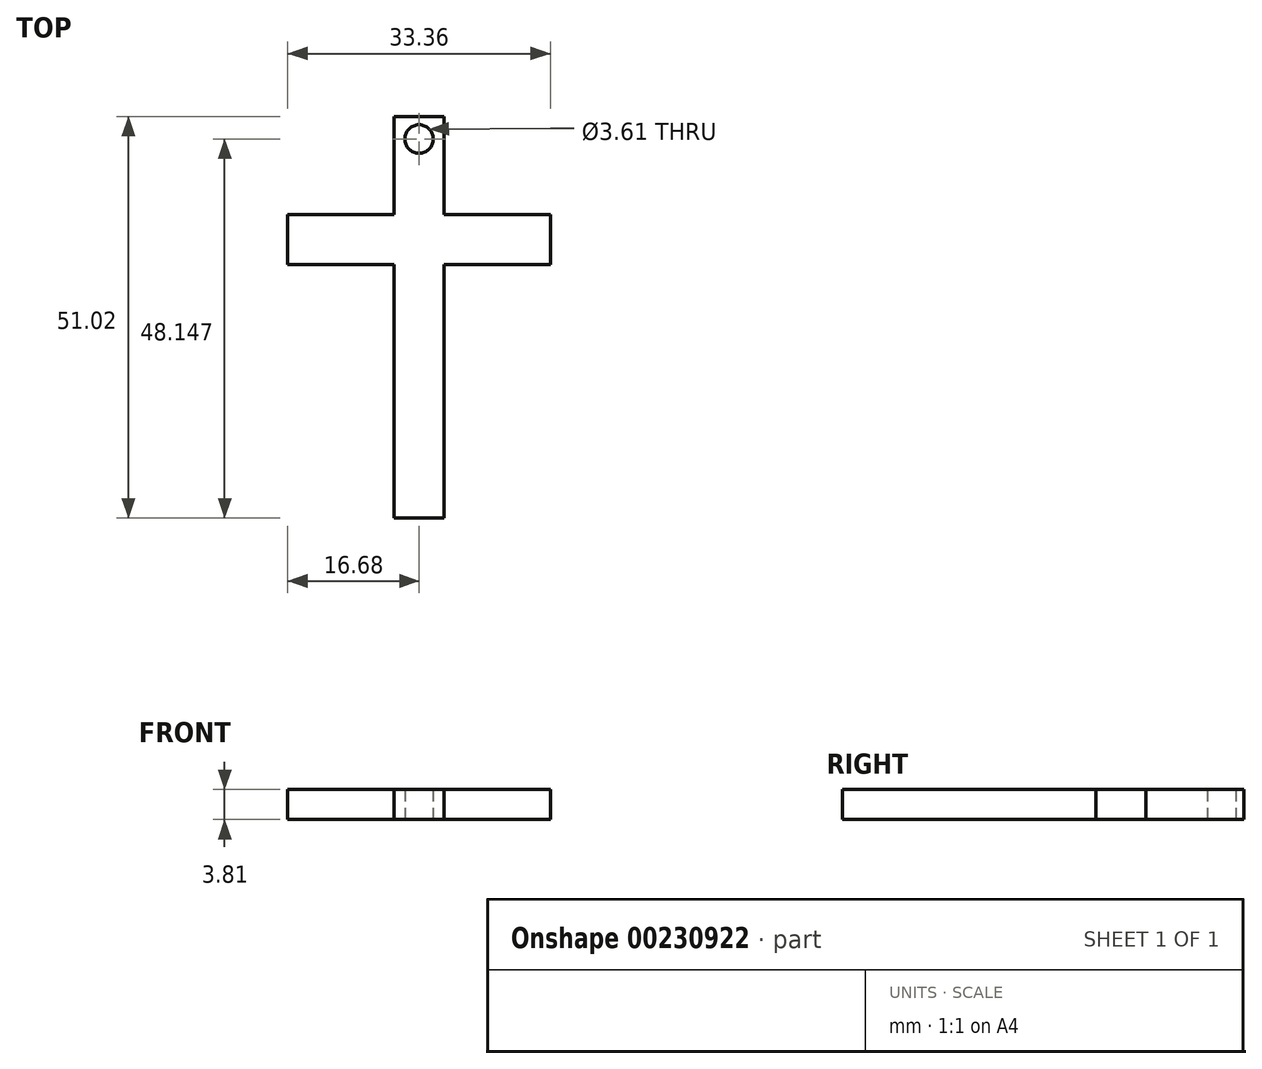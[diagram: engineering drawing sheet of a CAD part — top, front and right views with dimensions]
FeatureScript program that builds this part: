
annotation { "Feature Type Name" : "Feature", "Feature Type Description" : "" }
export const myFeature = defineFeature(function(context is Context, id is Id, definition is map)
    precondition{}
    {
        {
            var Q0;
            Q0=qCreatedBy(makeId("Top.planeOp"),FACE);
            var sketch = newSketch(context, id + "F0", { "sketchPlane" : qUnion([Q0])});
            skLineSegment(sketch, "E0.bottom", {"start": v(-3.18, -25.5) * mm, "end": v(3.18, -25.5) * mm});
            skLineSegment(sketch, "E0.top", {"start": v(-3.18, 25.5) * mm, "end": v(3.18, 25.5) * mm});
            skLineSegment(sketch, "E0.left", {"start": v(-3.18, -25.5) * mm, "end": v(-3.18, 25.5) * mm});
            skLineSegment(sketch, "E0.right", {"start": v(3.18, -25.5) * mm, "end": v(3.18, 25.5) * mm});
            skPoint(sketch, "E0.middle", {"position": v(0, 0) * mm});
            skLineSegment(sketch, "E1.bottom", {"start": v(16.68, 6.7) * mm, "end": v(-16.68, 6.7) * mm});
            skLineSegment(sketch, "E1.top", {"start": v(16.68, 13.04) * mm, "end": v(-16.68, 13.04) * mm});
            skLineSegment(sketch, "E1.left", {"start": v(16.68, 6.7) * mm, "end": v(16.68, 13.04) * mm});
            skLineSegment(sketch, "E1.right", {"start": v(-16.68, 6.7) * mm, "end": v(-16.68, 13.04) * mm});
            skPoint(sketch, "E1.middle", {"position": v(0, 9.87) * mm});
            skCircle(sketch, "E2", {"center": v(0, 22.64) * mm, "radius": 1.8 * mm});
            skSolve(sketch);
        }
        {
            var Q0;
            Q0 = qSketchRegion(id + "F0", true);
            extrude(context, id + "F1", {"entities" : qUnion([Q0]), "depth" : 3.8 * mm});
        }
    });
